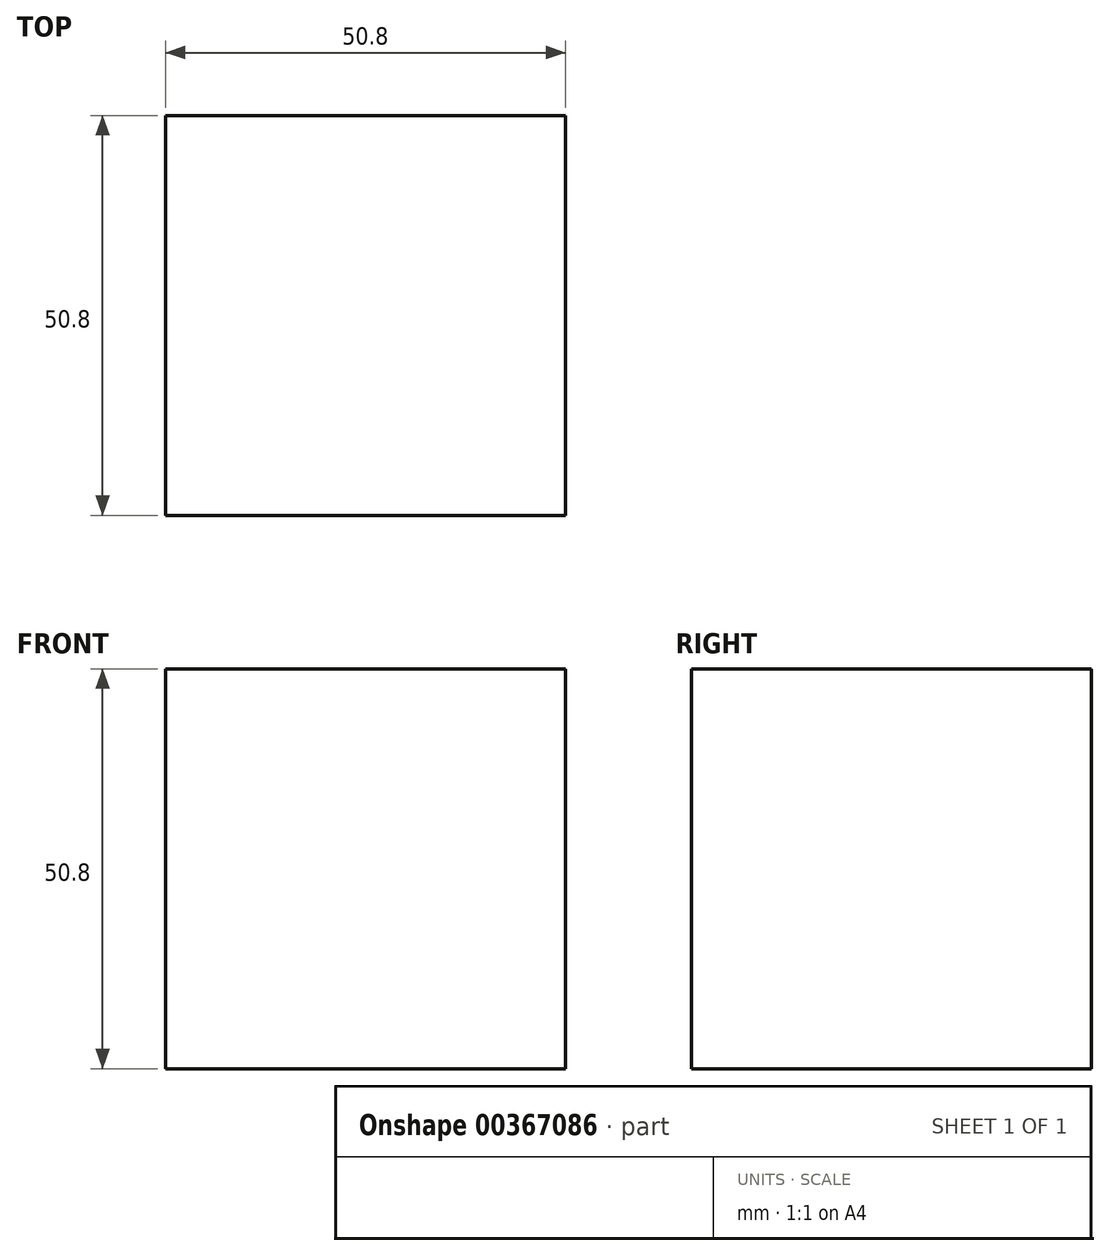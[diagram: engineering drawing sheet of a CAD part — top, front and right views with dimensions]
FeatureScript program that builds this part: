
annotation { "Feature Type Name" : "Feature", "Feature Type Description" : "" }
export const myFeature = defineFeature(function(context is Context, id is Id, definition is map)
    precondition{}
    {
        {
            var Q0;
            Q0=qCreatedBy(makeId("Top.planeOp"),FACE);
            var sketch = newSketch(context, id + "F0", { "sketchPlane" : qUnion([Q0])});
            skLineSegment(sketch, "E0.bottom", {"start": v(25.4, -25.4) * mm, "end": v(-25.4, -25.4) * mm});
            skLineSegment(sketch, "E0.top", {"start": v(25.4, 25.4) * mm, "end": v(-25.4, 25.4) * mm});
            skLineSegment(sketch, "E0.left", {"start": v(25.4, -25.4) * mm, "end": v(25.4, 25.4) * mm});
            skLineSegment(sketch, "E0.right", {"start": v(-25.4, -25.4) * mm, "end": v(-25.4, 25.4) * mm});
            skPoint(sketch, "E0.middle", {"position": v(0, 0) * mm});
            skSolve(sketch);
        }
        {
            var Q0;
            Q0=makeQuery(id+"F0.imprint","IMPRINT",FACE,{"disambiguationData":[TD([[makeQuery(id+"F0.imprint","IMPRINT",EDGE,{"derivedFrom":sQuery(id+"F0.wireOp",EDGE,"E0.bottom")}),-1.0]])]});
            extrude(context, id + "F1", {"entities" : qUnion([Q0]), "depth" : 50.8 * mm});
        }
    });
